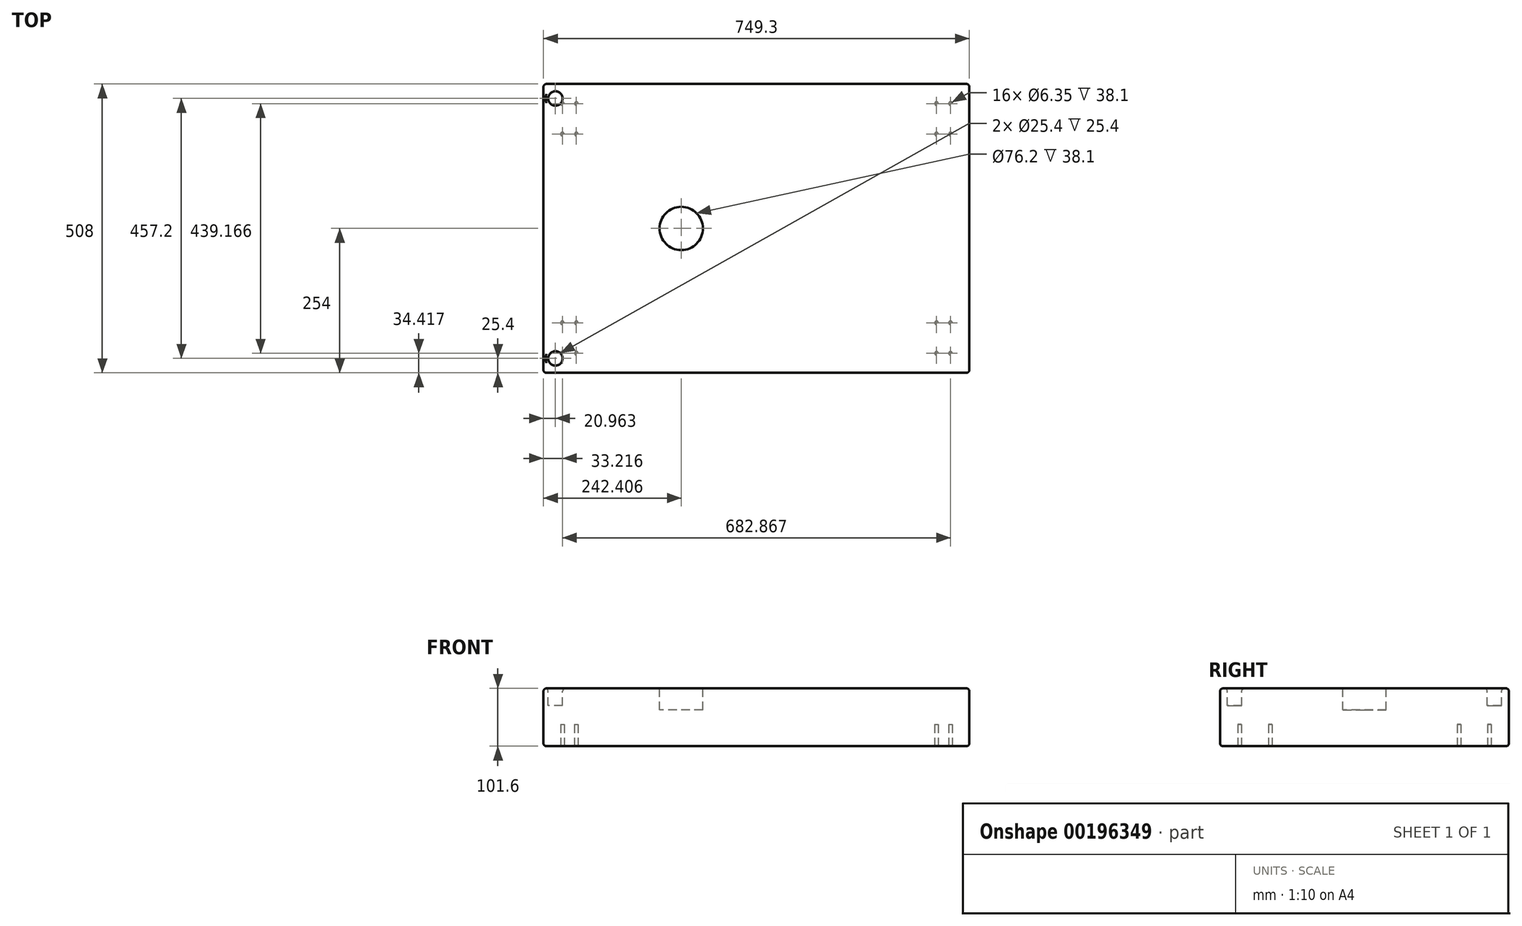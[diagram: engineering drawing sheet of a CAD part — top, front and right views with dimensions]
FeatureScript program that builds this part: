
annotation { "Feature Type Name" : "Feature", "Feature Type Description" : "" }
export const myFeature = defineFeature(function(context is Context, id is Id, definition is map)
    precondition{}
    {
        {
            var Q0;
            Q0=qCreatedBy(makeId("Top.planeOp"),FACE);
            var sketch = newSketch(context, id + "F0", { "sketchPlane" : qUnion([Q0])});
            skLineSegment(sketch, "E0.bottom", {"start": v(374.65, -254) * mm, "end": v(-374.65, -254) * mm});
            skLineSegment(sketch, "E0.top", {"start": v(374.65, 254) * mm, "end": v(-374.65, 254) * mm});
            skLineSegment(sketch, "E0.left", {"start": v(374.65, -254) * mm, "end": v(374.65, 254) * mm});
            skLineSegment(sketch, "E0.right", {"start": v(-374.65, -254) * mm, "end": v(-374.65, 254) * mm});
            skPoint(sketch, "E0.middle", {"position": v(0, 0) * mm});
            skSolve(sketch);
        }
        {
            var Q0;
            Q0 = qSketchRegion(id + "F0", true);
            extrude(context, id + "F1", {"entities" : qUnion([Q0]), "oppositeDirection" : true, "depth" : 101.6 * mm});
        }
        {
            var Q0;
            Q0=makeQuery(id+"F1.opExtrude","CAP_FACE",FACE,{"disambiguationData":[OSD([sQuery(id+"F0.wireOp",EDGE,"E0.bottom"),sQuery(id+"F0.wireOp",EDGE,"E0.top"),sQuery(id+"F0.wireOp",EDGE,"E0.left"),sQuery(id+"F0.wireOp",EDGE,"E0.right")])],"isStart":true});
            var sketch = newSketch(context, id + "F2", { "sketchPlane" : qUnion([Q0])});
            skCircle(sketch, "E1", {"center": v(-353.69, 228.6) * mm, "radius": 12.7 * mm});
            skLineSegment(sketch, "E2", {"start": v(0, 0) * mm, "end": v(-374.65, 0) * mm});
            skCircle(sketch, "E3.MirrorC", {"center": v(-353.69, -228.6) * mm, "radius": 12.7 * mm});
            skLineSegment(sketch, "E4", {"start": v(-353.69, 228.6) * mm, "end": v(-353.69, -228.6) * mm});
            skSolve(sketch);
        }
        {
            var Q0;
            Q0 = qSketchRegion(id + "F2", true);
            extrude(context, id + "F3", {"entities" : qUnion([Q0]), "operationType" : NewBodyOperationType.REMOVE, "oppositeDirection" : true, "depth" : 30.48 * mm});
        }
        {
            var Q0;
            Q0=makeQuery(id+"F1.opExtrude","CAP_FACE",FACE,{"disambiguationData":[OSD([sQuery(id+"F0.wireOp",EDGE,"E0.bottom"),sQuery(id+"F0.wireOp",EDGE,"E0.top"),sQuery(id+"F0.wireOp",EDGE,"E0.left"),sQuery(id+"F0.wireOp",EDGE,"E0.right")])],"isStart":true});
            var Q1;
            Q1=makeQuery(id+"F1.opExtrude","CAP_FACE",FACE,{"disambiguationData":[OSD([sQuery(id+"F0.wireOp",EDGE,"E0.bottom"),sQuery(id+"F0.wireOp",EDGE,"E0.top"),sQuery(id+"F0.wireOp",EDGE,"E0.left"),sQuery(id+"F0.wireOp",EDGE,"E0.right")])],"isStart":false});
            var Q2;
            Q2=makeQuery(id+"F1.opExtrude","SWEPT_FACE",FACE,{"disambiguationData":[OSD([sQuery(id+"F0.wireOp",EDGE,"E0.right")])]});
            var Q3;
            Q3=makeQuery(id+"F1.opExtrude","SWEPT_EDGE",EDGE,{"disambiguationData":[OSD([sQuery(id+"F0.wireOp",EDGE,"E0.bottom"),sQuery(id+"F0.wireOp",EDGE,"E0.left")])]});
            var Q4;
            Q4=makeQuery(id+"F1.opExtrude","SWEPT_EDGE",EDGE,{"disambiguationData":[OSD([sQuery(id+"F0.wireOp",EDGE,"E0.top"),sQuery(id+"F0.wireOp",EDGE,"E0.left")])]});
            fillet(context, id + "F4", {"entities" : qUnion([Q0, Q1, Q2, Q3, Q4]), "radius" : 5.08 * mm, "tangentPropagation" : true, "allowEdgeOverflow" : false});
        }
        {
            var Q0;
            Q0=makeQuery(id+"F1.opExtrude","CAP_FACE",FACE,{"disambiguationData":[OSD([sQuery(id+"F0.wireOp",EDGE,"E0.bottom"),sQuery(id+"F0.wireOp",EDGE,"E0.top"),sQuery(id+"F0.wireOp",EDGE,"E0.left"),sQuery(id+"F0.wireOp",EDGE,"E0.right")])],"isStart":false});
            var sketch = newSketch(context, id + "F5", { "sketchPlane" : qUnion([Q0])});
            skLineSegment(sketch, "E5", {"start": v(0, 0) * mm, "end": v(0, 248.92) * mm});
            skLineSegment(sketch, "E6", {"start": v(0, 0) * mm, "end": v(0, -248.92) * mm});
            skCircle(sketch, "E7", {"center": v(-341.43, 219.58) * mm, "radius": 3.18 * mm});
            skCircle(sketch, "E8", {"center": v(-316.8, 219.58) * mm, "radius": 3.18 * mm});
            skPoint(sketch, "E9.start.orphan", {"position": v(0, 223.52) * mm});
            skCircle(sketch, "E10", {"center": v(-341.43, 165.99) * mm, "radius": 3.18 * mm});
            skCircle(sketch, "E11", {"center": v(-316.8, 165.99) * mm, "radius": 3.18 * mm});
            skLineSegment(sketch, "E12", {"start": v(0, 0) * mm, "end": v(-369.57, 0) * mm});
            skLineSegment(sketch, "E13", {"start": v(0, 0) * mm, "end": v(369.57, 0) * mm});
            skCircle(sketch, "E14.MirrorC", {"center": v(-341.43, -219.58) * mm, "radius": 3.18 * mm});
            skCircle(sketch, "E15.MirrorC", {"center": v(-316.8, -219.58) * mm, "radius": 3.18 * mm});
            skCircle(sketch, "E16.MirrorC", {"center": v(-316.8, -165.99) * mm, "radius": 3.18 * mm});
            skCircle(sketch, "E17.MirrorC", {"center": v(-341.43, -165.99) * mm, "radius": 3.18 * mm});
            skCircle(sketch, "E18.MirrorC", {"center": v(341.43, 165.99) * mm, "radius": 3.18 * mm});
            skCircle(sketch, "E19.MirrorC", {"center": v(316.8, 165.99) * mm, "radius": 3.18 * mm});
            skCircle(sketch, "E20.MirrorC", {"center": v(316.8, 219.58) * mm, "radius": 3.18 * mm});
            skCircle(sketch, "E21.MirrorC", {"center": v(341.43, 219.58) * mm, "radius": 3.18 * mm});
            skCircle(sketch, "E22.MirrorC", {"center": v(316.8, -165.99) * mm, "radius": 3.18 * mm});
            skCircle(sketch, "E23.MirrorC", {"center": v(341.43, -165.99) * mm, "radius": 3.18 * mm});
            skCircle(sketch, "E24.MirrorC", {"center": v(316.8, -219.58) * mm, "radius": 3.18 * mm});
            skCircle(sketch, "E25.MirrorC", {"center": v(341.43, -219.58) * mm, "radius": 3.18 * mm});
            skLineSegment(sketch, "E26", {"start": v(-316.8, 165.99) * mm, "end": v(0, 165.99) * mm});
            skSolve(sketch);
        }
        {
            var Q0;
            Q0 = qSketchRegion(id + "F5", true);
            extrude(context, id + "F6", {"entities" : qUnion([Q0]), "operationType" : NewBodyOperationType.REMOVE, "oppositeDirection" : true, "depth" : 38.1 * mm});
        }
        {
            var Q0;
            Q0=makeQuery(id+"F4.opFillet","SPLIT",FACE,{"disambiguationData":[OD(2.0)],"derivedFrom":makeQuery(id+"F1.opExtrude","CAP_FACE",FACE,{"disambiguationData":[OSD([sQuery(id+"F0.wireOp",EDGE,"E0.bottom"),sQuery(id+"F0.wireOp",EDGE,"E0.top"),sQuery(id+"F0.wireOp",EDGE,"E0.left"),sQuery(id+"F0.wireOp",EDGE,"E0.right")])],"isStart":true})});
            var sketch = newSketch(context, id + "F7", { "sketchPlane" : qUnion([Q0])});
            skCircle(sketch, "E27", {"center": v(-132.24, 0) * mm, "radius": 38.1 * mm});
            skSolve(sketch);
        }
        {
            var Q0;
            Q0 = qSketchRegion(id + "F7", true);
            extrude(context, id + "F8", {"entities" : qUnion([Q0]), "operationType" : NewBodyOperationType.REMOVE, "oppositeDirection" : true, "depth" : 38.1 * mm});
        }
    });
